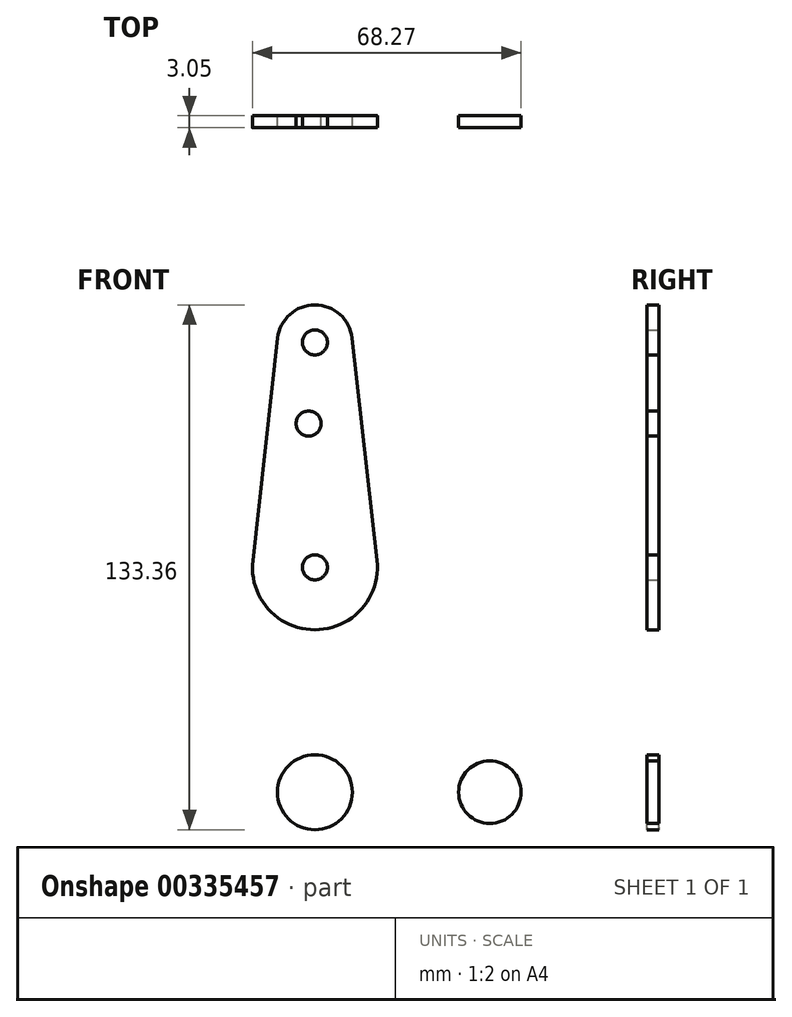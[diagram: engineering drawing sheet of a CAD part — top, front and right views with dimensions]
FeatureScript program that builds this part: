
annotation { "Feature Type Name" : "Feature", "Feature Type Description" : "" }
export const myFeature = defineFeature(function(context is Context, id is Id, definition is map)
    precondition{}
    {
        {
            var Q0;
            Q0=qCreatedBy(makeId("Front.planeOp"),FACE);
            var sketch = newSketch(context, id + "F0", { "sketchPlane" : qUnion([Q0])});
            skLineSegment(sketch, "E0", {"start": v(0, 114.3) * mm, "end": v(0, 0) * mm, "construction": true});
            skLineSegment(sketch, "E1", {"start": v(0, 0) * mm, "end": v(44.45, 0) * mm, "construction": true});
            skCircle(sketch, "E2", {"center": v(0, 114.3) * mm, "radius": 9.53 * mm});
            skCircle(sketch, "E3", {"center": v(0, 57.15) * mm, "radius": 15.88 * mm});
            skCircle(sketch, "E4", {"center": v(0, 0) * mm, "radius": 9.53 * mm});
            skCircle(sketch, "E5", {"center": v(44.45, 0) * mm, "radius": 7.94 * mm});
            skLineSegment(sketch, "E6", {"start": v(-9.47, 115.36) * mm, "end": v(-15.78, 58.91) * mm});
            skLineSegment(sketch, "E7", {"start": v(9.47, 115.36) * mm, "end": v(15.78, 58.91) * mm});
            skCircle(sketch, "E8", {"center": v(0, 114.3) * mm, "radius": 3.18 * mm});
            skCircle(sketch, "E9", {"center": v(0, 57.15) * mm, "radius": 3.18 * mm});
            skCircle(sketch, "E10", {"center": v(0, 0) * mm, "radius": 3.18 * mm});
            skCircle(sketch, "E11", {"center": v(44.45, 0) * mm, "radius": 3.18 * mm});
            skCircle(sketch, "E12", {"center": v(-1.59, 93.68) * mm, "radius": 3.18 * mm});
            skLineSegment(sketch, "E13", {"start": v(-9.52, 0) * mm, "end": v(-15.78, 55.39) * mm});
            skLineSegment(sketch, "E14", {"start": v(11.52, 17.68) * mm, "end": v(15.77, 55.37) * mm});
            skLineSegment(sketch, "E15", {"start": v(0, -9.53) * mm, "end": v(44.73, -7.93) * mm});
            skLineSegment(sketch, "E16", {"start": v(19.14, 8.84) * mm, "end": v(44.73, 7.93) * mm});
            skArc(sketch, "E17.filletArc", {"start": v(11.52, 17.68) * mm, "mid": v(13.4, 11.6) * mm, "end": v(19.14, 8.84) * mm});
            skSolve(sketch);
        }
        {
            var Q0;
            Q0 = qSketchRegion(id + "F0", true);
            extrude(context, id + "F1", {"entities" : qUnion([Q0]), "depth" : 3.05 * mm});
        }
    });
